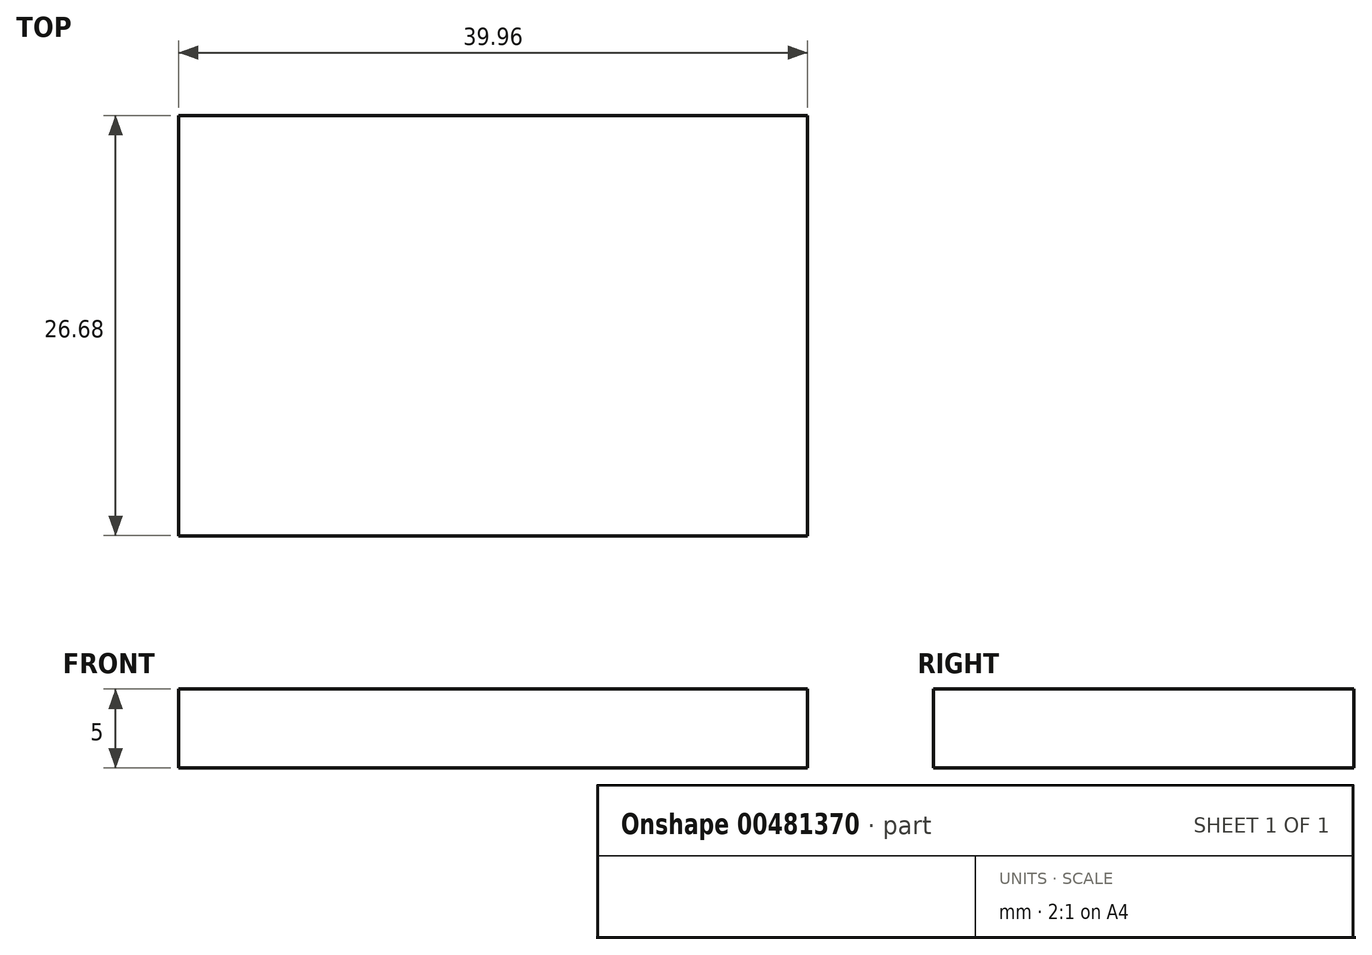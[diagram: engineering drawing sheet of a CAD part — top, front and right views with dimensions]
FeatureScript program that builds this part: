
annotation { "Feature Type Name" : "Feature", "Feature Type Description" : "" }
export const myFeature = defineFeature(function(context is Context, id is Id, definition is map)
    precondition{}
    {
        {
            var Q0;
            Q0=qCreatedBy(makeId("Top.planeOp"),FACE);
            var sketch = newSketch(context, id + "F0", { "sketchPlane" : qUnion([Q0])});
            skLineSegment(sketch, "E0.bottom", {"start": v(-31.21, 17.72) * mm, "end": v(8.75, 17.72) * mm});
            skLineSegment(sketch, "E0.top", {"start": v(-31.21, -8.96) * mm, "end": v(8.75, -8.96) * mm});
            skLineSegment(sketch, "E0.left", {"start": v(-31.21, 17.72) * mm, "end": v(-31.21, -8.96) * mm});
            skLineSegment(sketch, "E0.right", {"start": v(8.75, 17.72) * mm, "end": v(8.75, -8.96) * mm});
            skSolve(sketch);
        }
        {
            var Q0;
            Q0 = qSketchRegion(id + "F0", true);
            extrude(context, id + "F1", {"entities" : qUnion([Q0]), "depth" : 5 * mm});
        }
    });
